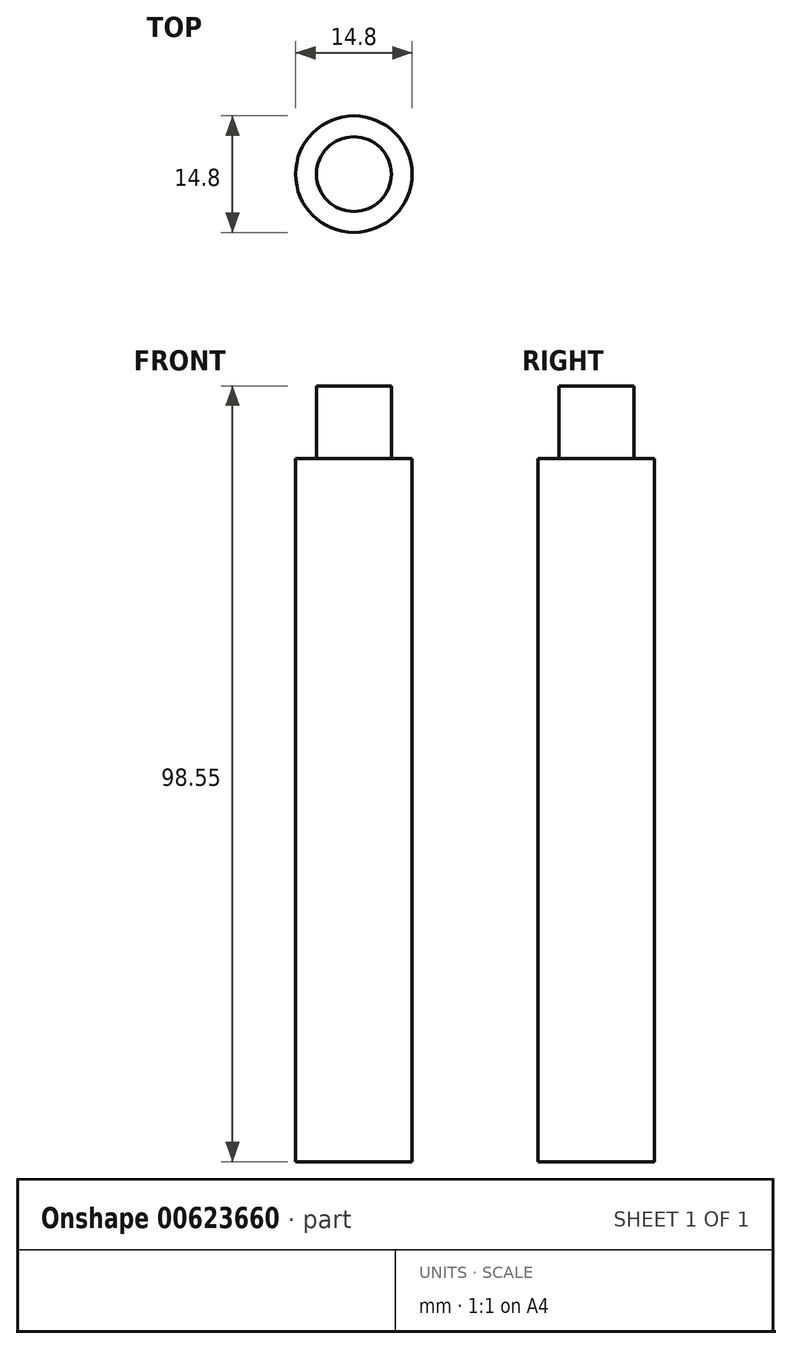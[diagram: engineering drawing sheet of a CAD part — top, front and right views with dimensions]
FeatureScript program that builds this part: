
annotation { "Feature Type Name" : "Feature", "Feature Type Description" : "" }
export const myFeature = defineFeature(function(context is Context, id is Id, definition is map)
    precondition{}
    {
        {
            var Q0;
            Q0=qCreatedBy(makeId("Top.planeOp"),FACE);
            var sketch = newSketch(context, id + "F0", { "sketchPlane" : qUnion([Q0])});
            skCircle(sketch, "E0", {"center": v(0, 0) * mm, "radius": 7.4 * mm});
            skSolve(sketch);
        }
        {
            var Q0;
            Q0=qSketchRegion(id+"F0",true);
            extrude(context, id + "F1", {"entities" : qUnion([Q0]), "depth" : 89.3 * mm, "offsetDistance" : 25 * mm});
        }
        {
            var Q0;
            Q0=makeQuery(id+"F1.opExtrude","CAP_FACE",FACE,{"disambiguationData":[OSD([sQuery(id+"F0.wireOp",EDGE,"E0")])],"isStart":false});
            var sketch = newSketch(context, id + "F2", { "sketchPlane" : qUnion([Q0])});
            skCircle(sketch, "E1", {"center": v(0, 0) * mm, "radius": 4.75 * mm});
            skSolve(sketch);
        }
        {
            var Q0;
            Q0=qSketchRegion(id+"F2",true);
            extrude(context, id + "F3", {"entities" : qUnion([Q0]), "operationType" : NewBodyOperationType.ADD, "depth" : 9.25 * mm, "offsetDistance" : 25 * mm});
        }
    });
